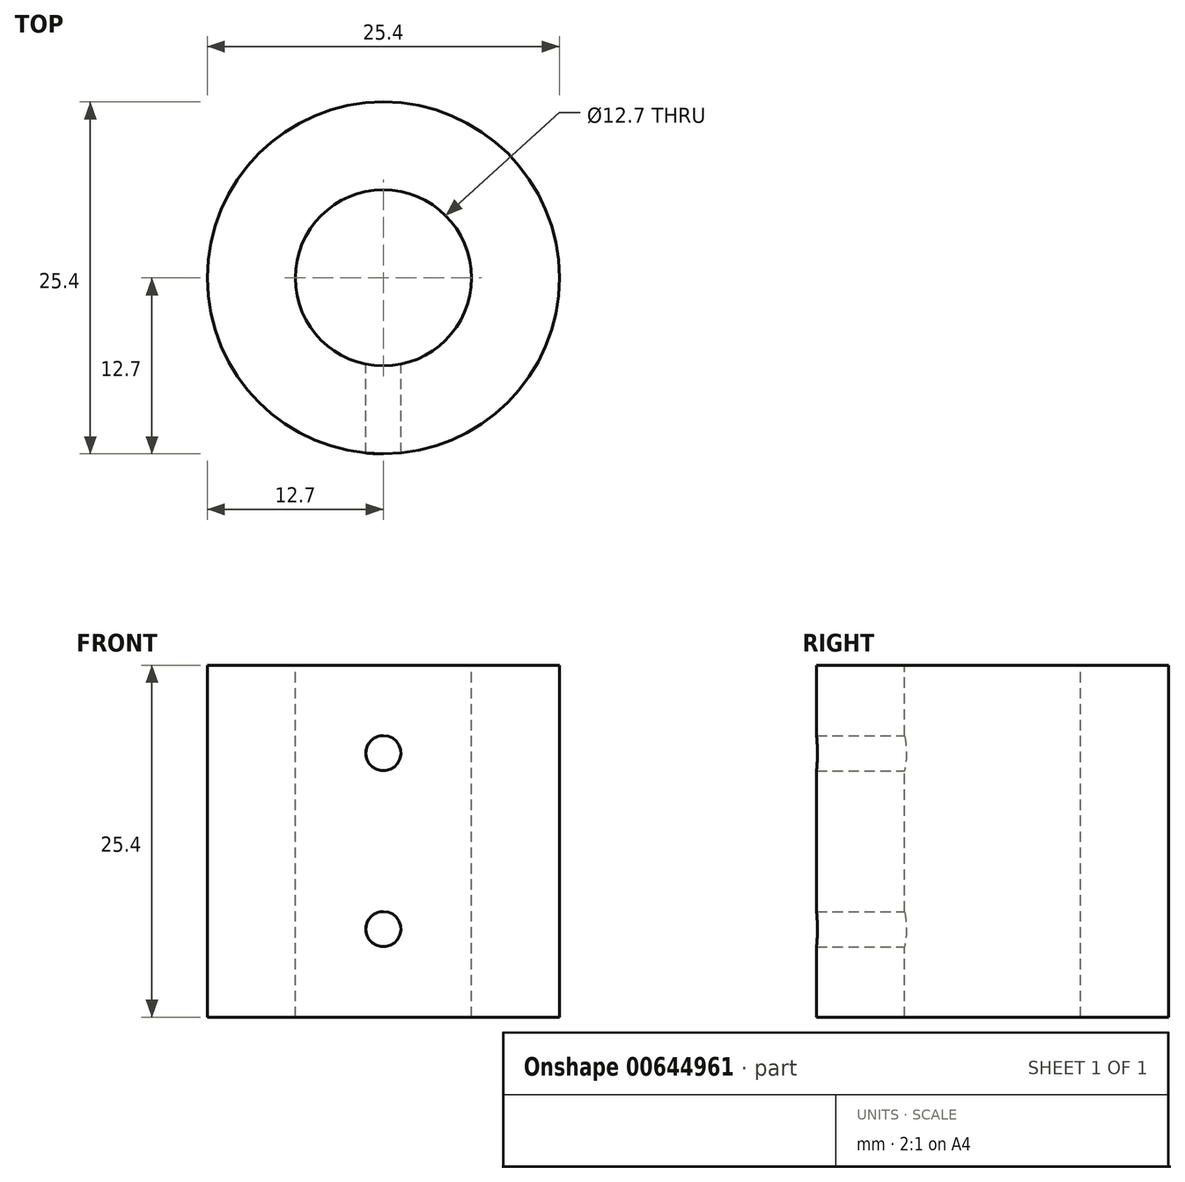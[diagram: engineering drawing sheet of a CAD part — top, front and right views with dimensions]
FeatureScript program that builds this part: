
annotation { "Feature Type Name" : "Feature", "Feature Type Description" : "" }
export const myFeature = defineFeature(function(context is Context, id is Id, definition is map)
    precondition{}
    {
        {
            var Q0;
            Q0=qCreatedBy(makeId("Top.planeOp"),FACE);
            var sketch = newSketch(context, id + "F0", { "sketchPlane" : qUnion([Q0])});
            skCircle(sketch, "E0", {"center": v(0, 0) * mm, "radius": 12.7 * mm});
            skSolve(sketch);
        }
        {
            var Q0;
            Q0=makeQuery(id+"F0.imprint","IMPRINT",FACE,{"disambiguationData":[TD([[makeQuery(id+"F0.imprint","IMPRINT",EDGE,{"derivedFrom":sQuery(id+"F0.wireOp",EDGE,"E0")}),1.0]])]});
            extrude(context, id + "F1", {"entities" : qUnion([Q0]), "depth" : 25.4 * mm, "offsetDistance" : 25.4 * mm});
        }
        {
            var Q0;
            Q0=makeQuery(id+"F1.opExtrude","CAP_FACE",FACE,{"disambiguationData":[OSD([sQuery(id+"F0.wireOp",EDGE,"E0")])],"isStart":false});
            var sketch = newSketch(context, id + "F2", { "sketchPlane" : qUnion([Q0])});
            skCircle(sketch, "E1", {"center": v(0, 0) * mm, "radius": 4.64 * mm});
            skSolve(sketch);
        }
        {
            var Q0;
            Q0=sQuery(id+"F2.wireOp",VERTEX,"E1.center");
            var Q1;
            Q1=makeQuery(id+"F1.opExtrude","SWEPT_BODY",BODY,{"disambiguationData":[OSD([sQuery(id+"F0.wireOp",EDGE,"E0")])]});
            hole(context, id + "F3", {"style" : HoleStyle.SIMPLE, "endStyle" : HoleEndStyle.THROUGH, "holeDiameter" : 12.7 * mm, "majorDiameter" : 6.35 * mm, "isTappedThrough" : true, "tappedDepth" : 12.7 * mm, "tapClearance" : 3, "locations" : qUnion([Q0]), "scope" : qUnion([Q1])});
        }
        {
            var Q0;
            Q0=qCreatedBy(makeId("Front.planeOp"),FACE);
            var sketch = newSketch(context, id + "F4", { "sketchPlane" : qUnion([Q0])});
            skCircle(sketch, "E2", {"center": v(0, 6.35) * mm, "radius": 1.27 * mm});
            skCircle(sketch, "E3", {"center": v(0, 19.05) * mm, "radius": 1.27 * mm});
            skSolve(sketch);
        }
        {
            var Q0;
            Q0 = qSketchRegion(id + "F4", true);
            extrude(context, id + "F5", {"entities" : qUnion([Q0]), "operationType" : NewBodyOperationType.REMOVE, "endBound" : BoundingType.THROUGH_ALL, "depth" : 25.4 * mm, "offsetDistance" : 25.4 * mm});
        }
    });
